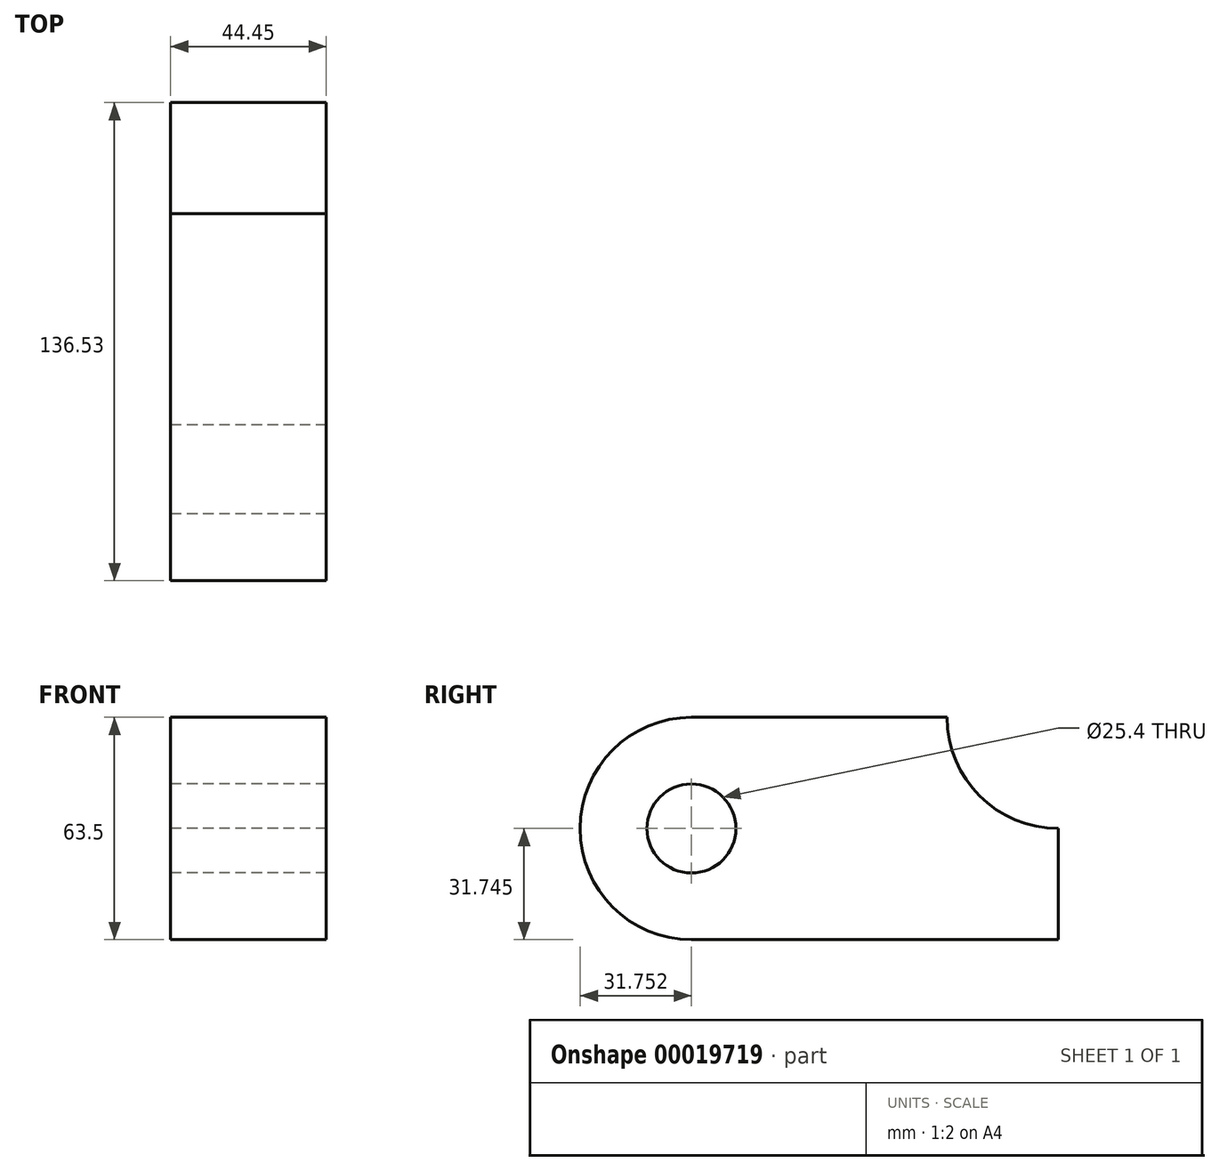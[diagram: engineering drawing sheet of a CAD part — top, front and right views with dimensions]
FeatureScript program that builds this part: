
annotation { "Feature Type Name" : "Feature", "Feature Type Description" : "" }
export const myFeature = defineFeature(function(context is Context, id is Id, definition is map)
    precondition{}
    {
        {
            var Q0;
            Q0=qCreatedBy(makeId("Right.planeOp"),FACE);
            var sketch = newSketch(context, id + "F0", { "sketchPlane" : qUnion([Q0])});
            skLineSegment(sketch, "E0.bottom", {"start": v(-24.76, 38) * mm, "end": v(48.27, 38) * mm});
            skLineSegment(sketch, "E0.top", {"start": v(-24.76, -25.5) * mm, "end": v(80.02, -25.5) * mm});
            skLineSegment(sketch, "E0.right", {"start": v(80.02, 6.25) * mm, "end": v(80.02, -25.5) * mm});
            skArc(sketch, "E1", {"start": v(48.27, 38) * mm, "mid": v(57.57, 15.54) * mm, "end": v(80.02, 6.25) * mm});
            skArc(sketch, "E2", {"start": v(-24.76, 38) * mm, "mid": v(-56.5, 6.25) * mm, "end": v(-24.76, -25.5) * mm});
            skCircle(sketch, "E3", {"center": v(-24.76, 6.25) * mm, "radius": 12.7 * mm});
            skSolve(sketch);
        }
        {
            var Q0;
            Q0=makeQuery(id+"F0.imprint","IMPRINT",FACE,{"disambiguationData":[TD([[makeQuery(id+"F0.imprint","IMPRINT",EDGE,{"derivedFrom":sQuery(id+"F0.wireOp",EDGE,"E0.bottom")}),-1.0]])]});
            extrude(context, id + "F1", {"entities" : qUnion([Q0]), "depth" : 44.45 * mm});
        }
    });
